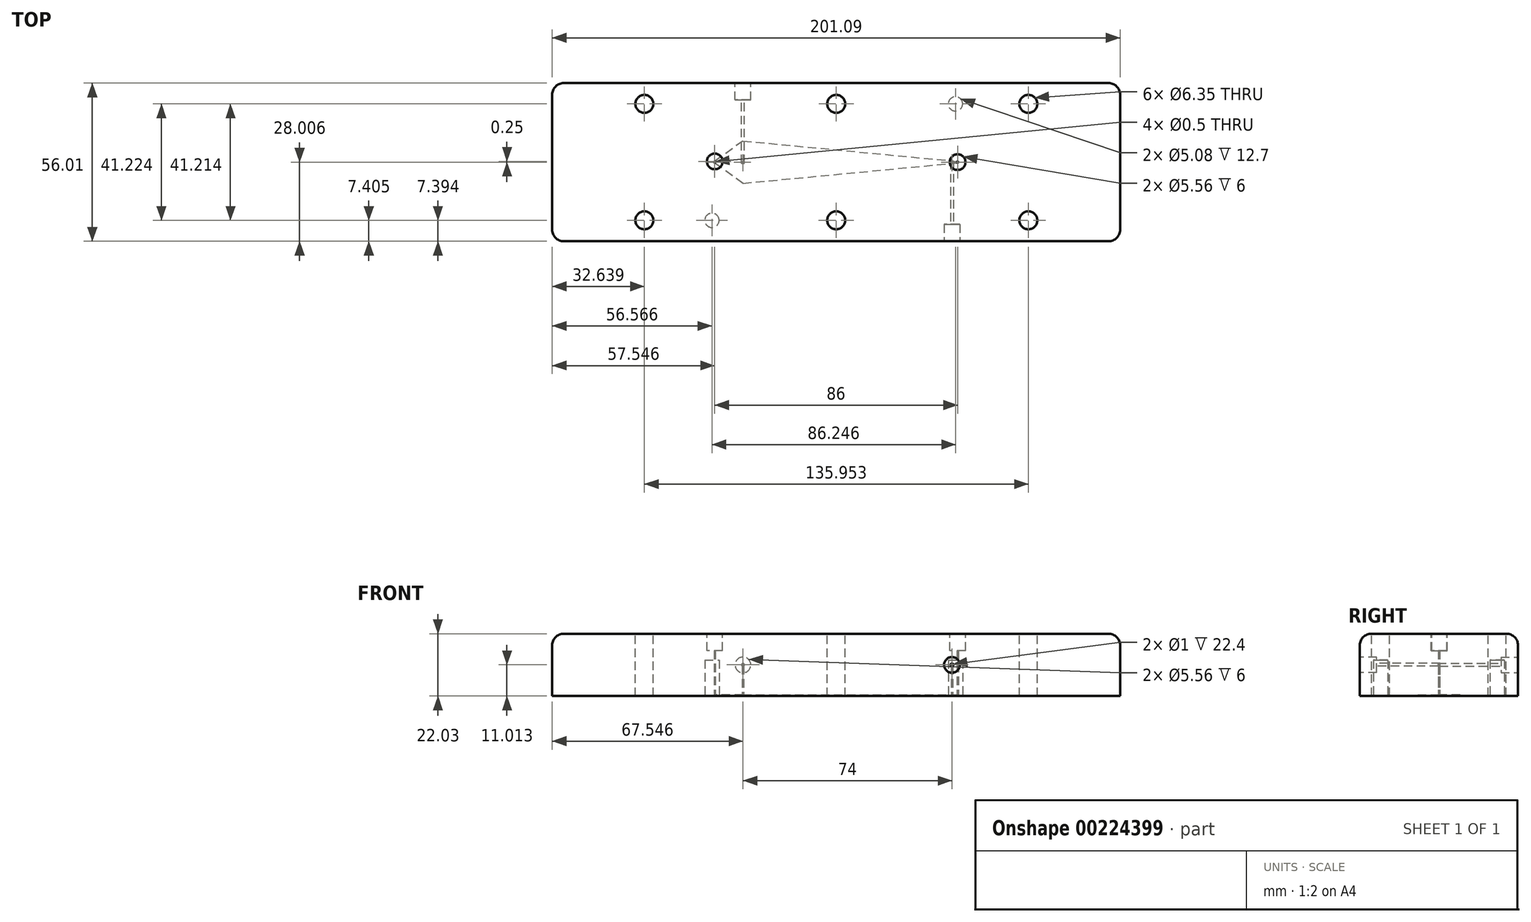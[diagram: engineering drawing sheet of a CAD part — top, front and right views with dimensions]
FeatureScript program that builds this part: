
annotation { "Feature Type Name" : "Feature", "Feature Type Description" : "" }
export const myFeature = defineFeature(function(context is Context, id is Id, definition is map)
    precondition{}
    {
        {
            var Q0;
            Q0=qCreatedBy(makeId("Top.planeOp"),FACE);
            var sketch = newSketch(context, id + "F0", { "sketchPlane" : qUnion([Q0])});
            skLineSegment(sketch, "E0.bottom", {"start": v(4.06, 0) * mm, "end": v(197.03, 0) * mm});
            skLineSegment(sketch, "E0.top", {"start": v(4.06, -56) * mm, "end": v(197.03, -56) * mm});
            skLineSegment(sketch, "E0.left", {"start": v(0, -4.06) * mm, "end": v(0, -51.94) * mm});
            skLineSegment(sketch, "E0.right", {"start": v(201.1, -4.06) * mm, "end": v(201.1, -51.94) * mm});
            skLineSegment(sketch, "E1.bottom", {"start": v(0, 0) * mm, "end": v(201.1, 0) * mm, "construction": true});
            skLineSegment(sketch, "E1.top", {"start": v(0, -7.4) * mm, "end": v(201.1, -7.4) * mm, "construction": true});
            skLineSegment(sketch, "E1.left", {"start": v(0, 0) * mm, "end": v(0, -7.4) * mm, "construction": true});
            skLineSegment(sketch, "E1.right", {"start": v(201.1, 0) * mm, "end": v(201.1, -7.4) * mm, "construction": true});
            skLineSegment(sketch, "E2.bottom", {"start": v(0, 0) * mm, "end": v(32.64, 0) * mm, "construction": true});
            skLineSegment(sketch, "E2.top", {"start": v(0, -56) * mm, "end": v(32.64, -56) * mm, "construction": true});
            skLineSegment(sketch, "E2.left", {"start": v(0, 0) * mm, "end": v(0, -56) * mm, "construction": true});
            skLineSegment(sketch, "E2.right", {"start": v(32.64, 0) * mm, "end": v(32.64, -56) * mm, "construction": true});
            skLineSegment(sketch, "E3.bottom", {"start": v(0, 0) * mm, "end": v(168.6, 0) * mm, "construction": true});
            skLineSegment(sketch, "E3.top", {"start": v(0, -56) * mm, "end": v(168.6, -56) * mm, "construction": true});
            skLineSegment(sketch, "E3.right", {"start": v(168.6, 0) * mm, "end": v(168.6, -56) * mm, "construction": true});
            skLineSegment(sketch, "E4.bottom", {"start": v(0, 0) * mm, "end": v(100.57, 0) * mm, "construction": true});
            skLineSegment(sketch, "E4.top", {"start": v(0, -56) * mm, "end": v(100.57, -56) * mm, "construction": true});
            skLineSegment(sketch, "E4.right", {"start": v(100.57, 0) * mm, "end": v(100.57, -56) * mm, "construction": true});
            skLineSegment(sketch, "E5.top", {"start": v(0, -48.6) * mm, "end": v(201.1, -48.6) * mm, "construction": true});
            skLineSegment(sketch, "E5.left", {"start": v(0, 0) * mm, "end": v(0, -48.6) * mm, "construction": true});
            skLineSegment(sketch, "E5.right", {"start": v(201.1, 0) * mm, "end": v(201.1, -48.6) * mm, "construction": true});
            skLineSegment(sketch, "E6.bottom", {"start": v(0, 0) * mm, "end": v(52.5, 0) * mm, "construction": true});
            skLineSegment(sketch, "E6.top", {"start": v(0, -56) * mm, "end": v(52.5, -56) * mm, "construction": true});
            skLineSegment(sketch, "E6.right", {"start": v(52.5, 0) * mm, "end": v(52.5, -56) * mm, "construction": true});
            skCircle(sketch, "E7", {"center": v(32.64, -7.4) * mm, "radius": 3.18 * mm});
            skCircle(sketch, "E8", {"center": v(100.57, -7.4) * mm, "radius": 3.18 * mm});
            skCircle(sketch, "E9", {"center": v(168.6, -7.4) * mm, "radius": 3.18 * mm});
            skCircle(sketch, "E10", {"center": v(168.6, -48.6) * mm, "radius": 3.18 * mm});
            skCircle(sketch, "E11", {"center": v(100.55, -48.6) * mm, "radius": 3.18 * mm});
            skCircle(sketch, "E12", {"center": v(32.64, -48.6) * mm, "radius": 3.18 * mm});
            skLineSegment(sketch, "E13.bottom", {"start": v(0, 0) * mm, "end": v(138.75, 0) * mm, "construction": true});
            skLineSegment(sketch, "E13.top", {"start": v(0, -56) * mm, "end": v(138.75, -56) * mm, "construction": true});
            skLineSegment(sketch, "E13.right", {"start": v(138.75, 0) * mm, "end": v(138.75, -56) * mm, "construction": true});
            skLineSegment(sketch, "E14.top", {"start": v(0, -56) * mm, "end": v(201.1, -56) * mm, "construction": true});
            skLineSegment(sketch, "E14.right", {"start": v(201.1, 0) * mm, "end": v(201.1, -56) * mm, "construction": true});
            skPoint(sketch, "E15.visualSharp", {"position": v(201.1, 0) * mm});
            skArc(sketch, "E15.filletArc", {"start": v(201.1, -4.06) * mm, "mid": v(199.9, -1.2) * mm, "end": v(197.03, 0) * mm});
            skPoint(sketch, "E16.visualSharp", {"position": v(0, -56) * mm});
            skArc(sketch, "E16.filletArc", {"start": v(0, -51.94) * mm, "mid": v(1.2, -54.82) * mm, "end": v(4.06, -56) * mm});
            skPoint(sketch, "E17.visualSharp", {"position": v(201.1, -56) * mm});
            skArc(sketch, "E17.filletArc", {"start": v(197.03, -56) * mm, "mid": v(199.9, -54.82) * mm, "end": v(201.1, -51.94) * mm});
            skPoint(sketch, "E18.visualSharp", {"position": v(0, 0) * mm});
            skArc(sketch, "E18.filletArc", {"start": v(4.06, 0) * mm, "mid": v(1.2, -1.2) * mm, "end": v(0, -4.06) * mm});
            skSolve(sketch);
        }
        {
            var Q0;
            Q0=qSketchRegion(id+"F0",true);
            extrude(context, id + "F1", {"entities" : qUnion([Q0]), "oppositeDirection" : true, "depth" : 22.03 * mm});
        }
        {
            var Q0;
            Q0=makeQuery(id+"F1.opExtrude","CAP_FACE",FACE,{"disambiguationData":[OSD([sQuery(id+"F0.wireOp",EDGE,"E0.bottom"),sQuery(id+"F0.wireOp",EDGE,"E0.top"),sQuery(id+"F0.wireOp",EDGE,"E0.left"),sQuery(id+"F0.wireOp",EDGE,"E0.right"),sQuery(id+"F0.wireOp",EDGE,"E7"),sQuery(id+"F0.wireOp",EDGE,"E8"),sQuery(id+"F0.wireOp",EDGE,"E9"),sQuery(id+"F0.wireOp",EDGE,"E10"),sQuery(id+"F0.wireOp",EDGE,"E11"),sQuery(id+"F0.wireOp",EDGE,"E12")])],"isStart":false});
            var sketch = newSketch(context, id + "F2", { "sketchPlane" : qUnion([Q0])});
            skLineSegment(sketch, "E19.bottom", {"start": v(4.06, 0) * mm, "end": v(201.1, 0) * mm, "construction": true});
            skLineSegment(sketch, "E19.top", {"start": v(4.06, 7.4) * mm, "end": v(201.1, 7.4) * mm, "construction": true});
            skLineSegment(sketch, "E19.left", {"start": v(4.06, 0) * mm, "end": v(4.06, 7.4) * mm, "construction": true});
            skLineSegment(sketch, "E19.right", {"start": v(201.1, 0) * mm, "end": v(201.1, 7.4) * mm, "construction": true});
            skLineSegment(sketch, "E20.top", {"start": v(4.06, 48.62) * mm, "end": v(201.1, 48.62) * mm, "construction": true});
            skLineSegment(sketch, "E20.left", {"start": v(4.06, 0) * mm, "end": v(4.06, 48.62) * mm, "construction": true});
            skLineSegment(sketch, "E20.right", {"start": v(201.1, 0) * mm, "end": v(201.1, 48.62) * mm, "construction": true});
            skLineSegment(sketch, "E21.bottom", {"start": v(4.06, 0) * mm, "end": v(56.57, 0) * mm, "construction": true});
            skLineSegment(sketch, "E21.top", {"start": v(4.06, 56) * mm, "end": v(56.57, 56) * mm, "construction": true});
            skLineSegment(sketch, "E21.left", {"start": v(4.06, 0) * mm, "end": v(4.06, 56) * mm, "construction": true});
            skLineSegment(sketch, "E21.right", {"start": v(56.57, 0) * mm, "end": v(56.57, 56) * mm, "construction": true});
            skLineSegment(sketch, "E22.bottom", {"start": v(4.06, 0) * mm, "end": v(142.81, 0) * mm, "construction": true});
            skLineSegment(sketch, "E22.top", {"start": v(4.06, 56) * mm, "end": v(142.81, 56) * mm, "construction": true});
            skLineSegment(sketch, "E22.right", {"start": v(142.81, 0) * mm, "end": v(142.81, 56) * mm, "construction": true});
            skCircle(sketch, "E23", {"center": v(56.57, 48.62) * mm, "radius": 2.54 * mm});
            skCircle(sketch, "E24", {"center": v(142.81, 7.4) * mm, "radius": 2.54 * mm});
            skSolve(sketch);
        }
        {
            var Q0;
            Q0=qSketchRegion(id+"F2",true);
            extrude(context, id + "F3", {"entities" : qUnion([Q0]), "operationType" : NewBodyOperationType.REMOVE, "oppositeDirection" : true, "depth" : 12.7 * mm});
        }
        {
            var Q0;
            Q0=qCreatedBy(makeId("Top.planeOp"),FACE);
            var sketch = newSketch(context, id + "F4", { "sketchPlane" : qUnion([Q0])});
            skLineSegment(sketch, "E25.bottom", {"start": v(0, 0) * mm, "end": v(201.1, 0) * mm, "construction": true});
            skLineSegment(sketch, "E25.top", {"start": v(0, -28) * mm, "end": v(201.1, -28) * mm, "construction": true});
            skLineSegment(sketch, "E25.left", {"start": v(0, 0) * mm, "end": v(0, -28) * mm, "construction": true});
            skLineSegment(sketch, "E25.right", {"start": v(201.1, 0) * mm, "end": v(201.1, -28) * mm, "construction": true});
            skLineSegment(sketch, "E26.bottom", {"start": v(0, 0) * mm, "end": v(13.06, 0) * mm, "construction": true});
            skLineSegment(sketch, "E26.top", {"start": v(0, -56) * mm, "end": v(13.06, -56) * mm, "construction": true});
            skLineSegment(sketch, "E26.left", {"start": v(0, 0) * mm, "end": v(0, -56) * mm, "construction": true});
            skLineSegment(sketch, "E26.right", {"start": v(13.06, 0) * mm, "end": v(13.06, -56) * mm, "construction": true});
            skLineSegment(sketch, "E27.bottom", {"start": v(0, 0) * mm, "end": v(32.7, 0) * mm, "construction": true});
            skLineSegment(sketch, "E27.top", {"start": v(0, -56) * mm, "end": v(32.7, -56) * mm, "construction": true});
            skLineSegment(sketch, "E27.right", {"start": v(32.7, 0) * mm, "end": v(32.7, -56) * mm, "construction": true});
            skLineSegment(sketch, "E28.bottom", {"start": v(0, 0) * mm, "end": v(185.05, 0) * mm, "construction": true});
            skLineSegment(sketch, "E28.top", {"start": v(0, -56) * mm, "end": v(185.05, -56) * mm, "construction": true});
            skLineSegment(sketch, "E28.right", {"start": v(185.05, 0) * mm, "end": v(185.05, -56) * mm, "construction": true});
            skCircle(sketch, "E29", {"center": v(185.05, -28) * mm, "radius": 2.78 * mm});
            skCircle(sketch, "E30", {"center": v(32.7, -28) * mm, "radius": 2.78 * mm});
            skCircle(sketch, "E31", {"center": v(13.06, -28) * mm, "radius": 2.78 * mm});
            skSolve(sketch);
        }
        {
            var Q0;
            Q0=makeQuery(id+"F1.opExtrude","CAP_FACE",FACE,{"disambiguationData":[OSD([sQuery(id+"F0.wireOp",EDGE,"E0.bottom"),sQuery(id+"F0.wireOp",EDGE,"E0.top"),sQuery(id+"F0.wireOp",EDGE,"E0.left"),sQuery(id+"F0.wireOp",EDGE,"E0.right"),sQuery(id+"F0.wireOp",EDGE,"E7"),sQuery(id+"F0.wireOp",EDGE,"E8"),sQuery(id+"F0.wireOp",EDGE,"E9"),sQuery(id+"F0.wireOp",EDGE,"E10"),sQuery(id+"F0.wireOp",EDGE,"E11"),sQuery(id+"F0.wireOp",EDGE,"E12"),sQuery(id+"F0.wireOp",EDGE,"E15.filletArc"),sQuery(id+"F0.wireOp",EDGE,"E16.filletArc"),sQuery(id+"F0.wireOp",EDGE,"E17.filletArc"),sQuery(id+"F0.wireOp",EDGE,"E18.filletArc")])],"isStart":false});
            var sketch = newSketch(context, id + "F5", { "sketchPlane" : qUnion([Q0])});
            skLineSegment(sketch, "E32.bottom", {"start": v(143.55, 20.5) * mm, "end": v(57.55, 20.5) * mm, "construction": true});
            skLineSegment(sketch, "E32.top", {"start": v(143.55, 35.5) * mm, "end": v(57.55, 35.5) * mm, "construction": true});
            skLineSegment(sketch, "E32.left", {"start": v(143.55, 20.5) * mm, "end": v(143.55, 27.75) * mm, "construction": true});
            skLineSegment(sketch, "E32.right", {"start": v(57.55, 20.5) * mm, "end": v(57.55, 35.5) * mm, "construction": true});
            skPoint(sketch, "E32.middle", {"position": v(100.55, 28) * mm});
            skPoint(sketch, "E32.middle.positionSnap0", {"position": v(100.55, 56) * mm});
            skPoint(sketch, "E32.middle.positionSnap1", {"position": v(0, 28) * mm});
            skPoint(sketch, "E32.centerSnap0", {"position": v(100.55, 56) * mm});
            skPoint(sketch, "E32.centerSnap1", {"position": v(0, 28) * mm});
            skLineSegment(sketch, "E33.bottom", {"start": v(57.55, 35.5) * mm, "end": v(67.55, 35.5) * mm, "construction": true});
            skLineSegment(sketch, "E33.top", {"start": v(57.55, 20.5) * mm, "end": v(67.55, 20.5) * mm, "construction": true});
            skLineSegment(sketch, "E33.left", {"start": v(57.55, 35.5) * mm, "end": v(57.55, 20.5) * mm, "construction": true});
            skArc(sketch, "E34", {"start": v(57.4, 28.2) * mm, "mid": v(57.3, 28) * mm, "end": v(57.4, 27.8) * mm});
            skLineSegment(sketch, "E35", {"start": v(67.55, 35.5) * mm, "end": v(57.4, 28.2) * mm});
            skLineSegment(sketch, "E36", {"start": v(67.55, 20.5) * mm, "end": v(57.4, 27.8) * mm});
            skLineSegment(sketch, "E37", {"start": v(67.55, 35.5) * mm, "end": v(143.55, 28.25) * mm});
            skLineSegment(sketch, "E38", {"start": v(67.55, 20.5) * mm, "end": v(143.55, 27.75) * mm});
            skLineSegment(sketch, "E39", {"start": v(143.55, 27.75) * mm, "end": v(143.55, 27.75) * mm});
            skArc(sketch, "E40", {"start": v(143.55, 27.75) * mm, "mid": v(143.8, 28) * mm, "end": v(143.55, 28.25) * mm});
            skLineSegment(sketch, "E41.trimOffspring", {"start": v(143.55, 28.25) * mm, "end": v(143.55, 35.5) * mm, "construction": true});
            skLineSegment(sketch, "E42.trimOffspring", {"start": v(143.55, 28.25) * mm, "end": v(143.55, 28.25) * mm});
            skSolve(sketch);
        }
        {
            var Q0;
            Q0 = qSketchRegion(id + "F5", true);
            extrude(context, id + "F6", {"entities" : qUnion([Q0]), "operationType" : NewBodyOperationType.REMOVE, "oppositeDirection" : true, "depth" : .45 * mm});
        }
        {
            var Q0;
            Q0=makeQuery(id+"F1.opExtrude","CAP_FACE",FACE,{"disambiguationData":[OSD([sQuery(id+"F0.wireOp",EDGE,"E0.bottom"),sQuery(id+"F0.wireOp",EDGE,"E0.top"),sQuery(id+"F0.wireOp",EDGE,"E0.left"),sQuery(id+"F0.wireOp",EDGE,"E0.right"),sQuery(id+"F0.wireOp",EDGE,"E7"),sQuery(id+"F0.wireOp",EDGE,"E8"),sQuery(id+"F0.wireOp",EDGE,"E9"),sQuery(id+"F0.wireOp",EDGE,"E10"),sQuery(id+"F0.wireOp",EDGE,"E11"),sQuery(id+"F0.wireOp",EDGE,"E12"),sQuery(id+"F0.wireOp",EDGE,"E15.filletArc"),sQuery(id+"F0.wireOp",EDGE,"E16.filletArc"),sQuery(id+"F0.wireOp",EDGE,"E17.filletArc"),sQuery(id+"F0.wireOp",EDGE,"E18.filletArc")])],"isStart":false});
            var sketch = newSketch(context, id + "F7", { "sketchPlane" : qUnion([Q0])});
            skLineSegment(sketch, "E43.bottom", {"start": v(143.55, 20.5) * mm, "end": v(57.55, 20.5) * mm, "construction": true});
            skLineSegment(sketch, "E43.top", {"start": v(143.55, 35.5) * mm, "end": v(57.55, 35.5) * mm, "construction": true});
            skLineSegment(sketch, "E43.left", {"start": v(143.55, 20.5) * mm, "end": v(143.55, 35.5) * mm, "construction": true});
            skLineSegment(sketch, "E43.right", {"start": v(57.55, 20.5) * mm, "end": v(57.55, 35.5) * mm, "construction": true});
            skPoint(sketch, "E43.middle", {"position": v(100.55, 28) * mm});
            skPoint(sketch, "E43.middle.positionSnap0", {"position": v(100.55, 56) * mm});
            skPoint(sketch, "E43.middle.positionSnap1", {"position": v(0, 28) * mm});
            skPoint(sketch, "E43.centerSnap0", {"position": v(100.55, 56) * mm});
            skPoint(sketch, "E43.centerSnap1", {"position": v(0, 28) * mm});
            skLineSegment(sketch, "E44.bottom", {"start": v(57.55, 35.5) * mm, "end": v(67.55, 35.5) * mm, "construction": true});
            skLineSegment(sketch, "E44.top", {"start": v(57.55, 20.5) * mm, "end": v(67.55, 20.5) * mm, "construction": true});
            skLineSegment(sketch, "E44.left", {"start": v(57.55, 35.5) * mm, "end": v(57.55, 20.5) * mm, "construction": true});
            skLineSegment(sketch, "E44.right", {"start": v(67.55, 35.5) * mm, "end": v(67.55, 20.5) * mm, "construction": true});
            skLineSegment(sketch, "E45.bottom", {"start": v(143.55, 35.5) * mm, "end": v(141.55, 35.5) * mm, "construction": true});
            skLineSegment(sketch, "E45.top", {"start": v(143.55, 20.5) * mm, "end": v(141.55, 20.5) * mm, "construction": true});
            skLineSegment(sketch, "E45.left", {"start": v(143.55, 35.5) * mm, "end": v(143.55, 20.5) * mm, "construction": true});
            skLineSegment(sketch, "E45.right", {"start": v(141.55, 35.5) * mm, "end": v(141.55, 20.5) * mm, "construction": true});
            skCircle(sketch, "E46", {"center": v(57.55, 28) * mm, "radius": 0.25 * mm});
            skPoint(sketch, "E46.centerSnap0", {"position": v(57.55, 28) * mm});
            skPoint(sketch, "E46.centerSnap1", {"position": v(57.3, 28) * mm});
            skPoint(sketch, "E47.centerSnap0", {"position": v(67.55, 28) * mm});
            skCircle(sketch, "E48", {"center": v(143.55, 28) * mm, "radius": 0.25 * mm});
            skSolve(sketch);
        }
        {
            var Q0;
            Q0 = qSketchRegion(id + "F7", true);
            extrude(context, id + "F8", {"entities" : qUnion([Q0]), "operationType" : NewBodyOperationType.REMOVE, "endBound" : BoundingType.THROUGH_ALL, "oppositeDirection" : true, "depth" : 8 * mm});
        }
        {
            var Q0;
            Q0=makeQuery(id+"F1.opExtrude","CAP_FACE",FACE,{"disambiguationData":[OSD([sQuery(id+"F0.wireOp",EDGE,"E0.bottom"),sQuery(id+"F0.wireOp",EDGE,"E0.top"),sQuery(id+"F0.wireOp",EDGE,"E0.left"),sQuery(id+"F0.wireOp",EDGE,"E0.right"),sQuery(id+"F0.wireOp",EDGE,"E7"),sQuery(id+"F0.wireOp",EDGE,"E8"),sQuery(id+"F0.wireOp",EDGE,"E9"),sQuery(id+"F0.wireOp",EDGE,"E10"),sQuery(id+"F0.wireOp",EDGE,"E11"),sQuery(id+"F0.wireOp",EDGE,"E12"),sQuery(id+"F0.wireOp",EDGE,"E15.filletArc"),sQuery(id+"F0.wireOp",EDGE,"E16.filletArc"),sQuery(id+"F0.wireOp",EDGE,"E17.filletArc"),sQuery(id+"F0.wireOp",EDGE,"E18.filletArc")])],"isStart":true});
            var sketch = newSketch(context, id + "F9", { "sketchPlane" : qUnion([Q0])});
            skLineSegment(sketch, "E49.bottom", {"start": v(143.55, -20.5) * mm, "end": v(57.55, -20.5) * mm, "construction": true});
            skLineSegment(sketch, "E49.top", {"start": v(143.55, -35.5) * mm, "end": v(57.55, -35.5) * mm, "construction": true});
            skLineSegment(sketch, "E49.left", {"start": v(143.55, -20.5) * mm, "end": v(143.55, -35.5) * mm, "construction": true});
            skLineSegment(sketch, "E49.right", {"start": v(57.55, -20.5) * mm, "end": v(57.55, -35.5) * mm, "construction": true});
            skPoint(sketch, "E49.middle", {"position": v(100.55, -28) * mm});
            skPoint(sketch, "E49.middle.positionSnap0", {"position": v(100.55, 0) * mm});
            skPoint(sketch, "E49.middle.positionSnap1", {"position": v(0, -28) * mm});
            skPoint(sketch, "E49.centerSnap0", {"position": v(100.55, 0) * mm});
            skPoint(sketch, "E49.centerSnap1", {"position": v(0, -28) * mm});
            skLineSegment(sketch, "E50.bottom", {"start": v(57.55, -20.5) * mm, "end": v(67.55, -20.5) * mm, "construction": true});
            skLineSegment(sketch, "E50.top", {"start": v(57.55, -35.5) * mm, "end": v(67.55, -35.5) * mm, "construction": true});
            skLineSegment(sketch, "E50.right", {"start": v(67.55, -20.5) * mm, "end": v(67.55, -35.5) * mm, "construction": true});
            skCircle(sketch, "E51", {"center": v(57.55, -27.75) * mm, "radius": 2.78 * mm});
            skPoint(sketch, "E51.centerSnap0", {"position": v(57.55, -28) * mm});
            skCircle(sketch, "E52", {"center": v(143.55, -28) * mm, "radius": 2.78 * mm});
            skSolve(sketch);
        }
        {
            var Q0;
            Q0 = qSketchRegion(id + "F9", true);
            extrude(context, id + "F10", {"entities" : qUnion([Q0]), "operationType" : NewBodyOperationType.REMOVE, "oppositeDirection" : true, "depth" : 6 * mm});
        }
        {
            var Q0;
            Q0=makeQuery(id+"F1.opExtrude","SWEPT_FACE",FACE,{"disambiguationData":[OSD([sQuery(id+"F0.wireOp",EDGE,"E0.top")])]});
            var sketch = newSketch(context, id + "F11", { "sketchPlane" : qUnion([Q0])});
            skLineSegment(sketch, "E53.bottom", {"start": v(143.55, -7.02) * mm, "end": v(57.55, -7.02) * mm, "construction": true});
            skLineSegment(sketch, "E53.top", {"start": v(143.55, -15.02) * mm, "end": v(57.55, -15.02) * mm, "construction": true});
            skLineSegment(sketch, "E53.left", {"start": v(143.55, -7.02) * mm, "end": v(143.55, -15.02) * mm, "construction": true});
            skLineSegment(sketch, "E53.right", {"start": v(57.55, -7.02) * mm, "end": v(57.55, -15.02) * mm, "construction": true});
            skPoint(sketch, "E53.middle", {"position": v(100.55, -11.02) * mm});
            skPoint(sketch, "E53.middle.positionSnap0", {"position": v(100.55, 0) * mm});
            skPoint(sketch, "E53.middle.positionSnap1", {"position": v(4.06, -11.02) * mm});
            skPoint(sketch, "E53.centerSnap0", {"position": v(100.55, 0) * mm});
            skPoint(sketch, "E53.centerSnap1", {"position": v(4.06, -11.02) * mm});
            skLineSegment(sketch, "E54.bottom", {"start": v(143.55, -7.02) * mm, "end": v(141.55, -7.02) * mm, "construction": true});
            skLineSegment(sketch, "E54.top", {"start": v(143.55, -15.02) * mm, "end": v(141.55, -15.02) * mm, "construction": true});
            skLineSegment(sketch, "E54.right", {"start": v(141.55, -7.02) * mm, "end": v(141.55, -15.02) * mm, "construction": true});
            skCircle(sketch, "E55", {"center": v(141.55, -11.02) * mm, "radius": 0.5 * mm});
            skSolve(sketch);
        }
        {
            var Q0;
            Q0 = qSketchRegion(id + "F11", true);
            extrude(context, id + "F12", {"entities" : qUnion([Q0]), "operationType" : NewBodyOperationType.REMOVE, "oppositeDirection" : true, "depth" : 28.4 * mm});
        }
        {
            var Q0;
            Q0=makeQuery(id+"F1.opExtrude","SWEPT_FACE",FACE,{"disambiguationData":[OSD([sQuery(id+"F0.wireOp",EDGE,"E0.top")])]});
            var sketch = newSketch(context, id + "F13", { "sketchPlane" : qUnion([Q0])});
            skLineSegment(sketch, "E56.bottom", {"start": v(143.55, -7.02) * mm, "end": v(57.55, -7.02) * mm, "construction": true});
            skLineSegment(sketch, "E56.top", {"start": v(143.55, -15.02) * mm, "end": v(57.55, -15.02) * mm, "construction": true});
            skLineSegment(sketch, "E56.left", {"start": v(143.55, -7.02) * mm, "end": v(143.55, -15.02) * mm, "construction": true});
            skLineSegment(sketch, "E56.right", {"start": v(57.55, -7.02) * mm, "end": v(57.55, -15.02) * mm, "construction": true});
            skPoint(sketch, "E56.middle", {"position": v(100.55, -11.02) * mm});
            skPoint(sketch, "E56.middle.positionSnap0", {"position": v(100.55, 0) * mm});
            skPoint(sketch, "E56.middle.positionSnap1", {"position": v(4.06, -11.02) * mm});
            skPoint(sketch, "E56.centerSnap0", {"position": v(100.55, 0) * mm});
            skPoint(sketch, "E56.centerSnap1", {"position": v(4.06, -11.02) * mm});
            skLineSegment(sketch, "E57.bottom", {"start": v(143.55, -7.02) * mm, "end": v(141.55, -7.02) * mm, "construction": true});
            skLineSegment(sketch, "E57.top", {"start": v(143.55, -15.02) * mm, "end": v(141.55, -15.02) * mm, "construction": true});
            skLineSegment(sketch, "E57.right", {"start": v(141.55, -7.02) * mm, "end": v(141.55, -15.02) * mm, "construction": true});
            skCircle(sketch, "E58", {"center": v(141.55, -11.02) * mm, "radius": 2.78 * mm});
            skSolve(sketch);
        }
        {
            var Q0;
            Q0 = qSketchRegion(id + "F13", true);
            extrude(context, id + "F14", {"entities" : qUnion([Q0]), "operationType" : NewBodyOperationType.REMOVE, "oppositeDirection" : true, "depth" : 6 * mm});
        }
        {
            var Q0;
            Q0=makeQuery(id+"F1.opExtrude","CAP_FACE",FACE,{"disambiguationData":[OSD([sQuery(id+"F0.wireOp",EDGE,"E0.bottom"),sQuery(id+"F0.wireOp",EDGE,"E0.top"),sQuery(id+"F0.wireOp",EDGE,"E0.left"),sQuery(id+"F0.wireOp",EDGE,"E0.right"),sQuery(id+"F0.wireOp",EDGE,"E7"),sQuery(id+"F0.wireOp",EDGE,"E8"),sQuery(id+"F0.wireOp",EDGE,"E9"),sQuery(id+"F0.wireOp",EDGE,"E10"),sQuery(id+"F0.wireOp",EDGE,"E11"),sQuery(id+"F0.wireOp",EDGE,"E12"),sQuery(id+"F0.wireOp",EDGE,"E15.filletArc"),sQuery(id+"F0.wireOp",EDGE,"E16.filletArc"),sQuery(id+"F0.wireOp",EDGE,"E17.filletArc"),sQuery(id+"F0.wireOp",EDGE,"E18.filletArc")])],"isStart":false});
            var sketch = newSketch(context, id + "F15", { "sketchPlane" : qUnion([Q0])});
            skLineSegment(sketch, "E59.bottom", {"start": v(143.55, 20.5) * mm, "end": v(57.55, 20.5) * mm, "construction": true});
            skLineSegment(sketch, "E59.top", {"start": v(143.55, 35.5) * mm, "end": v(57.55, 35.5) * mm, "construction": true});
            skLineSegment(sketch, "E59.left", {"start": v(143.55, 20.5) * mm, "end": v(143.55, 35.5) * mm, "construction": true});
            skLineSegment(sketch, "E59.right", {"start": v(57.55, 20.5) * mm, "end": v(57.55, 35.5) * mm, "construction": true});
            skPoint(sketch, "E59.middle", {"position": v(100.55, 28) * mm});
            skPoint(sketch, "E59.middle.positionSnap0", {"position": v(100.55, 56) * mm});
            skPoint(sketch, "E59.middle.positionSnap1", {"position": v(0, 28) * mm});
            skPoint(sketch, "E59.centerSnap0", {"position": v(100.55, 56) * mm});
            skPoint(sketch, "E59.centerSnap1", {"position": v(0, 28) * mm});
            skLineSegment(sketch, "E60.bottom", {"start": v(143.55, 35.5) * mm, "end": v(141.55, 35.5) * mm, "construction": true});
            skLineSegment(sketch, "E60.top", {"start": v(143.55, 20.5) * mm, "end": v(141.55, 20.5) * mm, "construction": true});
            skLineSegment(sketch, "E60.left", {"start": v(143.55, 35.5) * mm, "end": v(143.55, 20.5) * mm, "construction": true});
            skLineSegment(sketch, "E60.right", {"start": v(141.55, 35.5) * mm, "end": v(141.55, 20.5) * mm, "construction": true});
            skCircle(sketch, "E61", {"center": v(141.55, 28) * mm, "radius": 0.25 * mm});
            skLineSegment(sketch, "E62.bottom", {"start": v(57.55, 35.5) * mm, "end": v(67.55, 35.5) * mm, "construction": true});
            skLineSegment(sketch, "E62.top", {"start": v(57.55, 20.5) * mm, "end": v(67.55, 20.5) * mm, "construction": true});
            skLineSegment(sketch, "E62.left", {"start": v(57.55, 35.5) * mm, "end": v(57.55, 20.5) * mm, "construction": true});
            skLineSegment(sketch, "E62.right", {"start": v(67.55, 35.5) * mm, "end": v(67.55, 20.5) * mm, "construction": true});
            skCircle(sketch, "E63", {"center": v(67.55, 28) * mm, "radius": 0.25 * mm});
            skSolve(sketch);
        }
        {
            var Q0;
            Q0 = qSketchRegion(id + "F15", true);
            extrude(context, id + "F16", {"entities" : qUnion([Q0]), "operationType" : NewBodyOperationType.REMOVE, "oppositeDirection" : true, "depth" : 11 * mm});
        }
        {
            var Q0;
            Q0=makeQuery(id+"F1.opExtrude","SWEPT_FACE",FACE,{"disambiguationData":[OSD([sQuery(id+"F0.wireOp",EDGE,"E0.bottom")])]});
            var sketch = newSketch(context, id + "F17", { "sketchPlane" : qUnion([Q0])});
            skLineSegment(sketch, "E64.bottom", {"start": v(-67.55, -16.02) * mm, "end": v(-133.55, -16.02) * mm, "construction": true});
            skLineSegment(sketch, "E64.top", {"start": v(-67.55, -6.02) * mm, "end": v(-133.55, -6.02) * mm, "construction": true});
            skLineSegment(sketch, "E64.left", {"start": v(-67.55, -16.02) * mm, "end": v(-67.55, -6.02) * mm, "construction": true});
            skLineSegment(sketch, "E64.right", {"start": v(-133.55, -16.02) * mm, "end": v(-133.55, -6.02) * mm, "construction": true});
            skPoint(sketch, "E64.middle", {"position": v(-100.55, -11.02) * mm});
            skPoint(sketch, "E64.middle.positionSnap0", {"position": v(-100.55, 0) * mm});
            skPoint(sketch, "E64.middle.positionSnap1", {"position": v(-197.03, -11.02) * mm});
            skPoint(sketch, "E64.centerSnap0", {"position": v(-100.55, 0) * mm});
            skPoint(sketch, "E64.centerSnap1", {"position": v(-197.03, -11.02) * mm});
            skCircle(sketch, "E65", {"center": v(-67.55, -11.02) * mm, "radius": 0.5 * mm});
            skSolve(sketch);
        }
        {
            var Q0;
            Q0 = qSketchRegion(id + "F17", true);
            extrude(context, id + "F18", {"entities" : qUnion([Q0]), "operationType" : NewBodyOperationType.REMOVE, "oppositeDirection" : true, "depth" : 28.4 * mm});
        }
        {
            var Q0;
            Q0=makeQuery(id+"F1.opExtrude","SWEPT_FACE",FACE,{"disambiguationData":[OSD([sQuery(id+"F0.wireOp",EDGE,"E0.bottom")])]});
            var sketch = newSketch(context, id + "F19", { "sketchPlane" : qUnion([Q0])});
            skLineSegment(sketch, "E66.bottom", {"start": v(-67.55, -6.02) * mm, "end": v(-133.55, -6.02) * mm, "construction": true});
            skLineSegment(sketch, "E66.top", {"start": v(-67.55, -16.02) * mm, "end": v(-133.55, -16.02) * mm, "construction": true});
            skLineSegment(sketch, "E66.left", {"start": v(-67.55, -6.02) * mm, "end": v(-67.55, -16.02) * mm, "construction": true});
            skLineSegment(sketch, "E66.right", {"start": v(-133.55, -6.02) * mm, "end": v(-133.55, -16.02) * mm, "construction": true});
            skPoint(sketch, "E66.middle", {"position": v(-100.55, -11.02) * mm});
            skPoint(sketch, "E66.middle.positionSnap0", {"position": v(-100.55, 0) * mm});
            skPoint(sketch, "E66.middle.positionSnap1", {"position": v(-197.03, -11.02) * mm});
            skPoint(sketch, "E66.centerSnap0", {"position": v(-100.55, 0) * mm});
            skPoint(sketch, "E66.centerSnap1", {"position": v(-197.03, -11.02) * mm});
            skCircle(sketch, "E67", {"center": v(-67.55, -11.02) * mm, "radius": 2.78 * mm});
            skSolve(sketch);
        }
        {
            var Q0;
            Q0=makeQuery(id+"F1.opExtrude","CAP_EDGE",EDGE,{"disambiguationData":[OSD([sQuery(id+"F0.wireOp",EDGE,"E0.top")])],"isStart":true});
            var Q1;
            Q1=makeQuery(id+"F1.opExtrude","CAP_EDGE",EDGE,{"disambiguationData":[OSD([sQuery(id+"F0.wireOp",EDGE,"E17.filletArc")])],"isStart":true});
            var Q2;
            Q2=makeQuery(id+"F1.opExtrude","CAP_EDGE",EDGE,{"disambiguationData":[OSD([sQuery(id+"F0.wireOp",EDGE,"E0.right")])],"isStart":true});
            var Q3;
            Q3=makeQuery(id+"F1.opExtrude","CAP_EDGE",EDGE,{"disambiguationData":[OSD([sQuery(id+"F0.wireOp",EDGE,"E15.filletArc")])],"isStart":true});
            var Q4;
            Q4=makeQuery(id+"F1.opExtrude","CAP_EDGE",EDGE,{"disambiguationData":[OSD([sQuery(id+"F0.wireOp",EDGE,"E0.bottom")])],"isStart":true});
            var Q5;
            Q5=makeQuery(id+"F1.opExtrude","CAP_EDGE",EDGE,{"disambiguationData":[OSD([sQuery(id+"F0.wireOp",EDGE,"E18.filletArc")])],"isStart":true});
            var Q6;
            Q6=makeQuery(id+"F1.opExtrude","CAP_EDGE",EDGE,{"disambiguationData":[OSD([sQuery(id+"F0.wireOp",EDGE,"E0.left")])],"isStart":true});
            var Q7;
            Q7=makeQuery(id+"F1.opExtrude","CAP_EDGE",EDGE,{"disambiguationData":[OSD([sQuery(id+"F0.wireOp",EDGE,"E16.filletArc")])],"isStart":true});
            fillet(context, id + "F20", {"entities" : qUnion([Q0, Q1, Q2, Q3, Q4, Q5, Q6, Q7]), "radius" : 4.06 * mm, "tangentPropagation" : true, "allowEdgeOverflow" : false});
        }
        {
            var Q0;
            Q0 = qSketchRegion(id + "F19", true);
            extrude(context, id + "F21", {"entities" : qUnion([Q0]), "operationType" : NewBodyOperationType.REMOVE, "oppositeDirection" : true, "depth" : 6 * mm});
        }
    });
